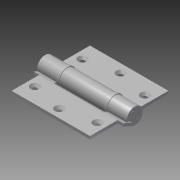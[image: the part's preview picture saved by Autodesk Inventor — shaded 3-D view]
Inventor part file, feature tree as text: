
AUTODESK INVENTOR PART (.ipt)
format: ipt  version: 2014 (Build 180170000, 170)  size: 240,640 bytes
history: native  units: in
note: dims shown in document units (in); Inventor stores cm internally (conversion verified against a paired STEP export)
features: imported_body x6, other x4, extrude x3
ambient origin geometry x8: Origin, YZ Plane, XZ Plane, XY Plane, X Axis, Y Axis, Z Axis, Center Point
bodies: Body1 (feature_tree), Body2 (feature_tree), Body3 (feature_tree), Body4 (feature_tree), Body5 (feature_tree), Body6 (feature_tree)
feature tree (13):
  other  "Cut-Extrude2"
  other  "8401A1701"
  extrude  "Extrude4"  [1 undecoded]
  other  "CSK for #10 Flat Head Machine Screw2[1]"
  other  "CSK for #10 Flat Head Machine Screw2[2]"
  extrude  "Extrude6"  [1 undecoded]
  extrude  "Extrude7"  [1 undecoded]
  imported_body  "Base1"
  imported_body  "Base2"
  imported_body  "Base3"
  imported_body  "Base4"
  imported_body  "Base5"
  imported_body  "Base6"
note: 3 required parameter values undecoded (feature->parameter linkage not recoverable at this tier; creation-order binding heuristic only, values carry confidence <= 0.55)
